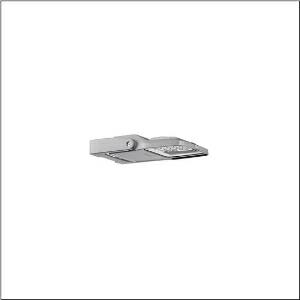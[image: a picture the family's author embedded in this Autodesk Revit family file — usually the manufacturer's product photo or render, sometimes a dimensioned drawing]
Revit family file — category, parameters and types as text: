
# Revit family: floodlight_fl_21_micro___pl33t_5xa7762a4f2a_51b5
name_source: partatom
category: Lighting Fixtures
units: mm (PartAtom-declared; Revit-internal decimal feet)

## family parameters
Cut with Voids When Loaded = No
Host = Face
Light Source = No
Part Type = Normal
Room Calculation Point = No
Round Connector Dimension = Use Diameter
Shared = No

## types (1)
- --- (1 x LED, 3050 lm, 23.1 W, 4000K)
    Apparent Load = 23 VA
    CIE Flux Codes = 26 75 99 100 100
    Color Rendering = 70
    Color Temperature = 4000K
    Default Elevation = 1800 mm
    Description = Floodlight FL 21 micro, floodlight, primary light control with lens, of PMMA, primary optical cover: protective disc, of toughened safety glass, transparent, light distribution: PL33T, light emission: direct distribution, installation type: surface-mounted, LED, High Power LED, rated luminous flux: 3.050lm, luminous efficacy: 132lm/W, light colour: 740, colour temperature: 4000K, control gear: ECG iQ, control: Auto-Match, Temp-Guard, Night-Set, Smart-Wire, Desk-Remote (wireless, voltage-free reading and setting of iQ features in the workshop via application-optimized NFC function/RFID function), optimised constant luminous flux control (CLO 2.0), Street-Remote, with terminal, 6-pole, mains connection: 220..240V, AC, 50/60Hz, start of lifetime: 23W, end of lifetime: 24W, reduction: 11W, luminaire housing, of diecast aluminium, powder-coated, Siteco® metallic grey (DB 702S), corrosivity category C5 according to DIN EN ISO 12944, design bracket, of diecast aluminium, powder-coated, Siteco® metallic grey (DB 702S), protection rating (complete): IP66, insulation class (complete): insulation class II (safety insulation), certification: CE, protection symbol: D, impact resistance: IK07, permissible operating ambient temperature: -40..+40°C, permissible operating ambient temperature for outdoor applications: -40..+50°C, standard: DIN EN 12944, packaging unit: 1 piece

Light Distribution: PL33T
    Height = 65 mm
    Lamp = 1 x LED
    Lamp Light Flux = 3050 lm
    Lamp Power = 23.1 W
    Lamp count = 1
    Length = 312 mm
    Luminous efficacy = 132 lm/W
    Manufacturer = Siteco
    ModVariant = No
    Model = 5XA7762A4F2A
    Number of Poles = 1
    OnlyDefault = Yes
    Power Factor = 1
    Product Name = Floodlight FL 21 micro | PL33T
    Product group = floodlight | pylon top
    ProductGroupID = 6101
    Protection Class = Protection class II
    Protection Degree = IP 66
    RLX_Detail_Level = 1
    RlxData = <blob elided: 97089 chars, md5=6f48c36d>
    Socket = socket
    Standby Power = 0 W
    System Light Flux = 3050 lm
    System Power = 23 W
    Type Comments = factory setting: luminous flux: 100 % | dim-lin: 254 | 455 mA
    Type Image = l_1006878.jpg
    URL = http://relux.com
    VarID = @adj_057991
    Voltage = 0 V
    Weight = 0.00 kg
    Width = 230 mm

## geometry (parser evidence)
native form markers: Blend x4, Sweep x12
no freeform markers — native parametric forms only
